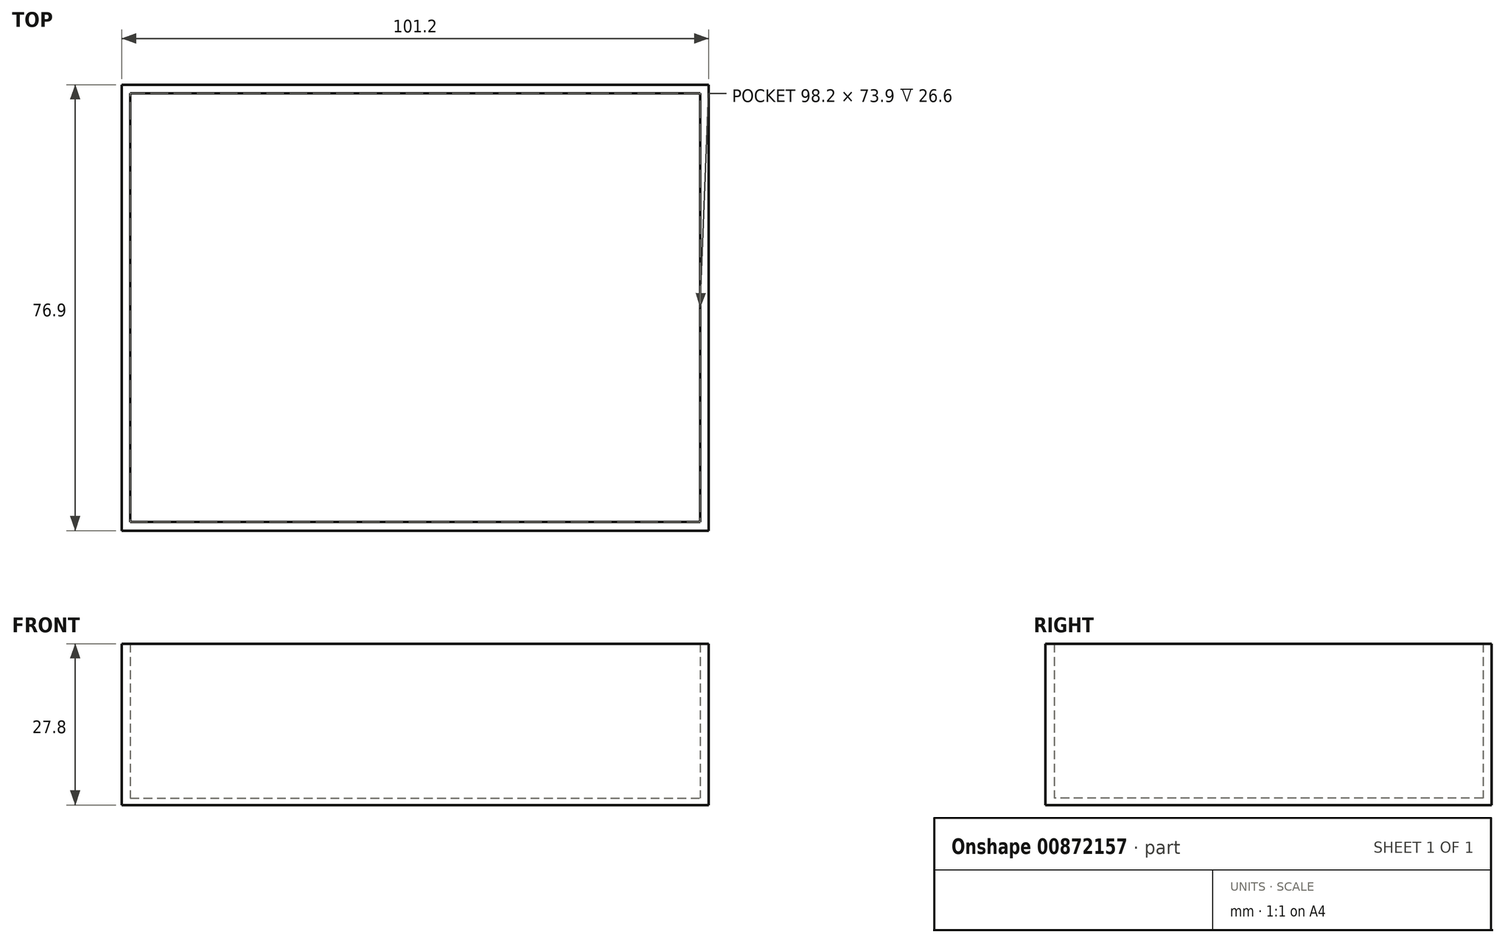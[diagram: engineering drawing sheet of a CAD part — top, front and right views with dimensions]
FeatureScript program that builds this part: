
annotation { "Feature Type Name" : "Feature", "Feature Type Description" : "" }
export const myFeature = defineFeature(function(context is Context, id is Id, definition is map)
    precondition{}
    {
        {
            var Q0;
            Q0=qCreatedBy(makeId("Top.planeOp"),FACE);
            var sketch = newSketch(context, id + "F0", { "sketchPlane" : qUnion([Q0])});
            skLineSegment(sketch, "E0.bottom", {"start": v(-49.1, 36.95) * mm, "end": v(49.1, 36.95) * mm});
            skLineSegment(sketch, "E0.top", {"start": v(-49.1, -36.95) * mm, "end": v(49.1, -36.95) * mm});
            skLineSegment(sketch, "E0.left", {"start": v(-49.1, 36.95) * mm, "end": v(-49.1, -36.95) * mm});
            skLineSegment(sketch, "E0.right", {"start": v(49.1, 36.95) * mm, "end": v(49.1, -36.95) * mm});
            skLineSegment(sketch, "E1", {"start": v(0, 63.1) * mm, "end": v(0, -64.8) * mm, "construction": true});
            skPoint(sketch, "E1.startSnap0", {"position": v(0, 36.95) * mm});
            skLineSegment(sketch, "E2", {"start": v(-65.65, 0) * mm, "end": v(53.75, 0) * mm, "construction": true});
            skPoint(sketch, "E2.startSnap0", {"position": v(-49.1, 0) * mm});
            skPoint(sketch, "E3", {"position": v(0, 0) * mm});
            skLineSegment(sketch, "E4.0", {"start": v(-50.6, 38.45) * mm, "end": v(50.6, 38.45) * mm});
            skLineSegment(sketch, "E4.1", {"start": v(-50.6, 38.45) * mm, "end": v(-50.6, -38.45) * mm});
            skLineSegment(sketch, "E4.2", {"start": v(-50.6, -38.45) * mm, "end": v(50.6, -38.45) * mm});
            skLineSegment(sketch, "E4.3", {"start": v(50.6, 38.45) * mm, "end": v(50.6, -38.45) * mm});
            skSolve(sketch);
        }
        {
            var Q0;
            Q0=makeQuery(id+"F0.imprint","IMPRINT",FACE,{"disambiguationData":[TD([[makeQuery(id+"F0.imprint","IMPRINT",EDGE,{"derivedFrom":sQuery(id+"F0.wireOp",EDGE,"E0.bottom")}),-1.0]])]});
            extrude(context, id + "F1", {"entities" : qUnion([Q0]), "depth" : 1.2 * mm, "offsetDistance" : 25 * mm});
        }
        {
            var Q0;
            Q0=makeQuery(id+"F0.imprint","IMPRINT",FACE,{"disambiguationData":[TD([[makeQuery(id+"F0.imprint","IMPRINT",EDGE,{"derivedFrom":sQuery(id+"F0.wireOp",EDGE,"E0.bottom")}),1.0]])]});
            extrude(context, id + "F2", {"entities" : qUnion([Q0]), "operationType" : NewBodyOperationType.ADD, "depth" : (23 + 1.8 + 3) * mm, "offsetDistance" : 25 * mm});
        }
    });
